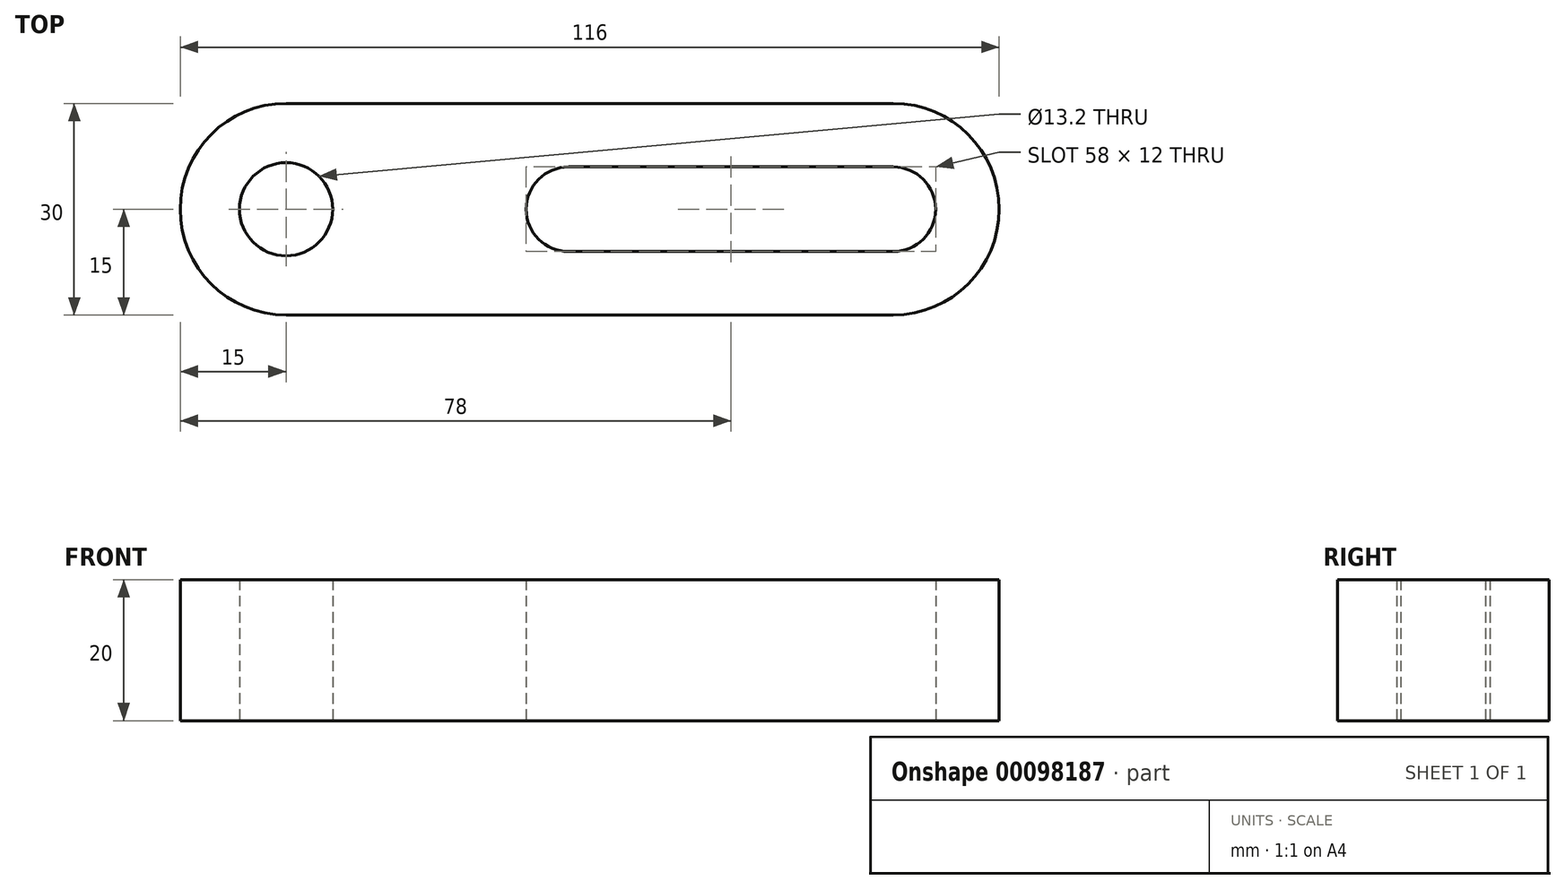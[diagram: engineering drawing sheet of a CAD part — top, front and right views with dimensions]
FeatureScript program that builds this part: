
annotation { "Feature Type Name" : "Feature", "Feature Type Description" : "" }
export const myFeature = defineFeature(function(context is Context, id is Id, definition is map)
    precondition{}
    {
        {
            var Q0;
            Q0=qCreatedBy(makeId("Top.planeOp"),FACE);
            var sketch = newSketch(context, id + "F0", { "sketchPlane" : qUnion([Q0])});
            skCircle(sketch, "E0", {"center": v(0, 0) * mm, "radius": 6 * mm});
            skLineSegment(sketch, "E1", {"start": v(0, 0) * mm, "end": v(46, 0) * mm});
            skCircle(sketch, "E2", {"center": v(46, 0) * mm, "radius": 6 * mm});
            skLineSegment(sketch, "E3", {"start": v(0, 6) * mm, "end": v(46, 6) * mm});
            skLineSegment(sketch, "E4", {"start": v(46, -6) * mm, "end": v(0, -6) * mm});
            skCircle(sketch, "E5", {"center": v(46, 0) * mm, "radius": 15 * mm});
            skLineSegment(sketch, "E6", {"start": v(46, 15) * mm, "end": v(-69.05, 15) * mm});
            skLineSegment(sketch, "E7", {"start": v(46, -15) * mm, "end": v(-69.36, -15) * mm});
            skLineSegment(sketch, "E8", {"start": v(0, 0) * mm, "end": v(-40, 0) * mm});
            skCircle(sketch, "E9", {"center": v(-40, 0) * mm, "radius": 15 * mm});
            skSolve(sketch);
        }
        {
            var Q0;
            Q0 = qSketchRegion(id + "F0", true);
            extrude(context, id + "F1", {"entities" : qUnion([Q0]), "depth" : 20 * mm, "offsetDistance" : 25 * mm});
        }
        {
            var Q0;
            Q0=makeQuery(id+"F1.opExtrude","CAP_FACE",FACE,{"disambiguationData":[OSD([sQuery(id+"F0.wireOp",EDGE,"E0"),sQuery(id+"F0.wireOp",EDGE,"E2"),sQuery(id+"F0.wireOp",EDGE,"E3"),sQuery(id+"F0.wireOp",EDGE,"E4"),sQuery(id+"F0.wireOp",EDGE,"E5"),sQuery(id+"F0.wireOp",EDGE,"E6"),sQuery(id+"F0.wireOp",EDGE,"E7"),sQuery(id+"F0.wireOp",EDGE,"E9")])],"isStart":false});
            var sketch = newSketch(context, id + "F2", { "sketchPlane" : qUnion([Q0])});
            skPoint(sketch, "E10", {"position": v(-40, 0) * mm});
            skSolve(sketch);
        }
        {
            var Q0;
            Q0=sQuery(id+"F2.wireOp",VERTEX,"E10");
            var Q1;
            Q1=makeQuery(id+"F1.opExtrude","SWEPT_BODY",BODY,{"disambiguationData":[OSD([sQuery(id+"F0.wireOp",EDGE,"E0"),sQuery(id+"F0.wireOp",EDGE,"E2"),sQuery(id+"F0.wireOp",EDGE,"E3"),sQuery(id+"F0.wireOp",EDGE,"E4"),sQuery(id+"F0.wireOp",EDGE,"E5"),sQuery(id+"F0.wireOp",EDGE,"E6"),sQuery(id+"F0.wireOp",EDGE,"E7"),sQuery(id+"F0.wireOp",EDGE,"E9")])]});
            hole(context, id + "F3", {"style" : HoleStyle.SIMPLE, "endStyle" : HoleEndStyle.THROUGH, "standardTappedOrClearance" : lookupTablePath({ "standard" : "ISO", "fit" : "Normal", "size" : "M12", "type" : "Clearance" }), "standardBlindInLast" : lookupTablePath({ "fit" : "Standard", "standard" : "ISO", "size" : "M12", "type" : "Clearance" }), "holeDiameter" : 13.2 * mm, "majorDiameter" : 5 * mm, "isTappedThrough" : true, "tappedDepth" : 12 * mm, "tapClearance" : 3, "locations" : qUnion([Q0]), "scope" : qUnion([Q1]), "startStyle" : HoleStartStyle.PART});
        }
    });
